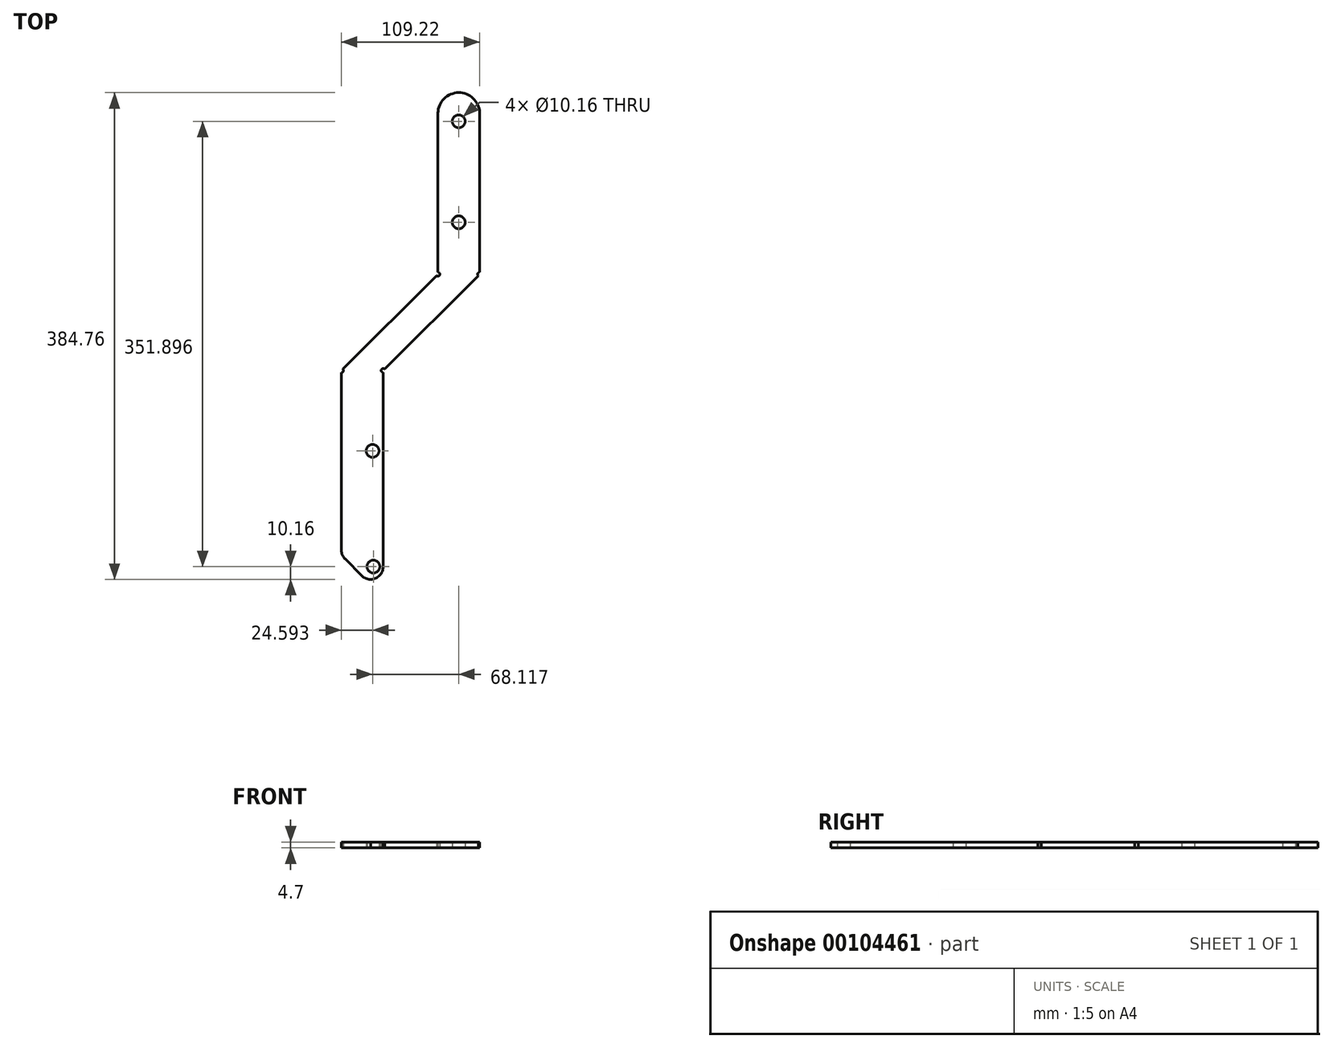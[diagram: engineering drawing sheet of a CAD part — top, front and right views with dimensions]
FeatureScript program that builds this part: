
annotation { "Feature Type Name" : "Feature", "Feature Type Description" : "" }
export const myFeature = defineFeature(function(context is Context, id is Id, definition is map)
    precondition{}
    {
        {
            var Q0;
            Q0=qCreatedBy(makeId("Top.planeOp"),FACE);
            var sketch = newSketch(context, id + "F0", { "sketchPlane" : qUnion([Q0])});
            skLineSegment(sketch, "E0", {"start": v(0, 165.1) * mm, "end": v(33.02, 165.1) * mm});
            skLineSegment(sketch, "E1", {"start": v(33.02, 165.1) * mm, "end": v(33.02, 0) * mm});
            skCircle(sketch, "E2", {"center": v(25.27, 10.16) * mm, "radius": 5.08 * mm});
            skCircle(sketch, "E3", {"center": v(24.6, 101.6) * mm, "radius": 5.08 * mm});
            skLineSegment(sketch, "E4", {"start": v(0, 19.05) * mm, "end": v(19.05, 0) * mm});
            skLineSegment(sketch, "E5", {"start": v(33.02, 0) * mm, "end": v(19.05, 0) * mm});
            skLineSegment(sketch, "E6", {"start": v(0, 19.05) * mm, "end": v(0, 165.1) * mm});
            skLineSegment(sketch, "E7", {"start": v(76.2, 241.3) * mm, "end": v(109.22, 241.3) * mm});
            skCircle(sketch, "E8", {"center": v(76.2, 241.3) * mm, "radius": 1.59 * mm});
            skCircle(sketch, "E9", {"center": v(109.22, 241.3) * mm, "radius": 1.59 * mm});
            skCircle(sketch, "E10", {"center": v(33.02, 165.1) * mm, "radius": 1.59 * mm});
            skCircle(sketch, "E11", {"center": v(0, 165.1) * mm, "radius": 1.59 * mm});
            skLineSegment(sketch, "E12", {"start": v(109.22, 241.3) * mm, "end": v(33.02, 165.1) * mm});
            skLineSegment(sketch, "E13", {"start": v(76.2, 241.3) * mm, "end": v(0, 165.1) * mm});
            skLineSegment(sketch, "E14", {"start": v(109.22, 241.3) * mm, "end": v(109.22, 393.7) * mm});
            skLineSegment(sketch, "E15", {"start": v(109.22, 393.7) * mm, "end": v(76.2, 393.7) * mm});
            skLineSegment(sketch, "E16", {"start": v(76.2, 393.7) * mm, "end": v(76.2, 241.3) * mm});
            skLineSegment(sketch, "E17", {"start": v(92.71, 393.7) * mm, "end": v(92.71, 241.3) * mm});
            skCircle(sketch, "E18", {"center": v(92.71, 362.06) * mm, "radius": 5.08 * mm});
            skCircle(sketch, "E19", {"center": v(92.71, 282.24) * mm, "radius": 5.08 * mm});
            skArc(sketch, "E20", {"start": v(109.22, 368.9) * mm, "mid": v(92.6, 384.76) * mm, "end": v(76.2, 368.66) * mm});
            skSolve(sketch);
        }
        {
            var Q0;
            Q0=makeQuery(id+"F0.imprint","IMPRINT",FACE,{"disambiguationData":[TD([[makeQuery(id+"F0.imprint","IMPRINT",EDGE,{"derivedFrom":sQuery(id+"F0.wireOp",EDGE,"E2")}),-1.0]])]});
            var Q1;
            {var subQ5=sQuery(id+"F0.wireOp",EDGE,"E17");var subQ9=sQuery(id+"F0.wireOp",EDGE,"E7");var subQ14=makeQuery(id+"F0.imprint","INTERSECT",VERTEX,{"derivedFrom":[subQ9,subQ5]});Q1=makeQuery(id+"F0.imprint","IMPRINT",FACE,{"disambiguationData":[TD([[makeQuery(id+"F0.imprint","IMPRINT",EDGE,{"disambiguationData":[TD([[subQ14,1.0]])],"derivedFrom":subQ9}),1.0]])]});}
            var Q2;
            {var subQ5=sQuery(id+"F0.wireOp",EDGE,"E7");var subQ7=sQuery(id+"F0.wireOp",EDGE,"E17");var subQ11=makeQuery(id+"F0.imprint","INTERSECT",VERTEX,{"derivedFrom":[subQ5,subQ7]});Q2=makeQuery(id+"F0.imprint","IMPRINT",FACE,{"disambiguationData":[TD([[makeQuery(id+"F0.imprint","IMPRINT",EDGE,{"disambiguationData":[TD([[subQ11,-1.0]])],"derivedFrom":subQ5}),1.0]])]});}
            var Q3;
            {var subQ8=sQuery(id+"F0.wireOp",EDGE,"E11");var subQ10=sQuery(id+"F0.wireOp",EDGE,"E0");var subQ11=makeQuery(id+"F0.imprint","INTERSECT",VERTEX,{"derivedFrom":[subQ10,subQ8]});Q3=makeQuery(id+"F0.imprint","IMPRINT",FACE,{"disambiguationData":[TD([[makeQuery(id+"F0.imprint","IMPRINT",EDGE,{"disambiguationData":[TD([[subQ11,-1.0]])],"derivedFrom":subQ10}),1.0]])]});}
            extrude(context, id + "F1", {"entities" : qUnion([Q0, Q1, Q2, Q3]), "depth" : 4.7 * mm});
        }
        {
            var Q0;
            Q0=makeQuery(id+"F1.opExtrude","SWEPT_EDGE",EDGE,{"disambiguationData":[OSD([sQuery(id+"F0.wireOp",EDGE,"E4"),sQuery(id+"F0.wireOp",EDGE,"E6")])]});
            var Q1;
            Q1=makeQuery(id+"F1.opExtrude","SWEPT_EDGE",EDGE,{"disambiguationData":[OSD([sQuery(id+"F0.wireOp",EDGE,"E4"),sQuery(id+"F0.wireOp",EDGE,"E5")])]});
            var Q2;
            Q2=makeQuery(id+"F1.opExtrude","SWEPT_EDGE",EDGE,{"disambiguationData":[OSD([sQuery(id+"F0.wireOp",EDGE,"E1"),sQuery(id+"F0.wireOp",EDGE,"E5")])]});
            fillet(context, id + "F2", {"entities" : qUnion([Q0, Q1, Q2]), "radius" : 10.16 * mm, "tangentPropagation" : true, "allowEdgeOverflow" : false});
        }
    });
